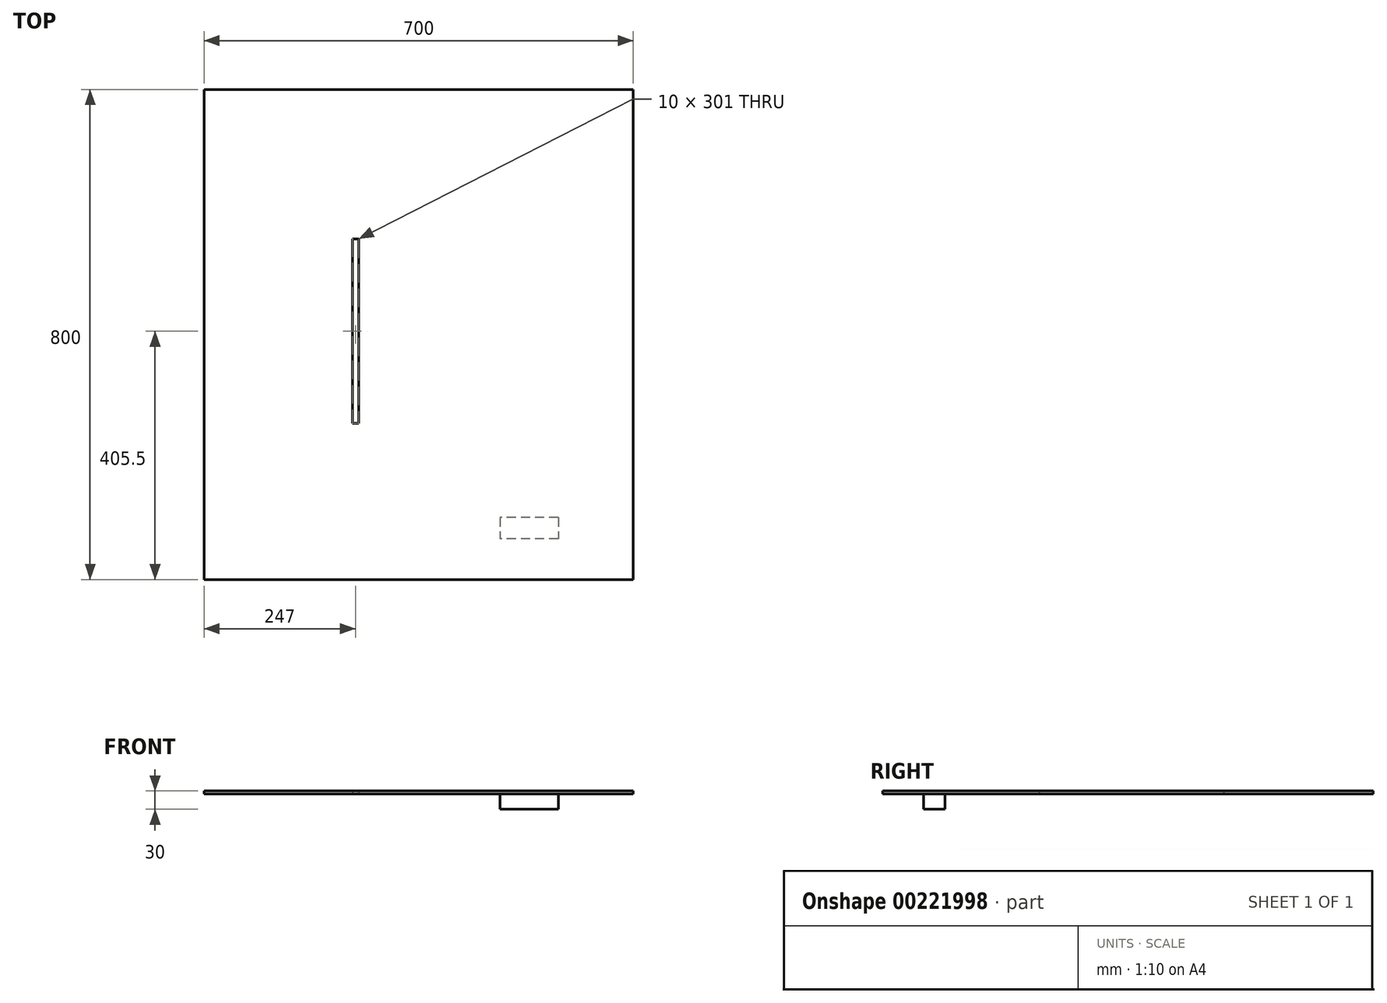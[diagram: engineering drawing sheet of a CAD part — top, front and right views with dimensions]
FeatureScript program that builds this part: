
annotation { "Feature Type Name" : "Feature", "Feature Type Description" : "" }
export const myFeature = defineFeature(function(context is Context, id is Id, definition is map)
    precondition{}
    {
        {
            var Q0;
            Q0=qCreatedBy(makeId("Top.planeOp"),FACE);
            var sketch = newSketch(context, id + "F0", { "sketchPlane" : qUnion([Q0])});
            skLineSegment(sketch, "E0.bottom", {"start": v(350, -400) * mm, "end": v(-350, -400) * mm});
            skLineSegment(sketch, "E0.top", {"start": v(350, 400) * mm, "end": v(-350, 400) * mm});
            skLineSegment(sketch, "E0.left", {"start": v(350, -400) * mm, "end": v(350, 400) * mm});
            skLineSegment(sketch, "E0.right", {"start": v(-350, -400) * mm, "end": v(-350, 400) * mm});
            skPoint(sketch, "E0.middle", {"position": v(0, 0) * mm});
            skLineSegment(sketch, "E1.bottom", {"start": v(-98, -145) * mm, "end": v(-108, -145) * mm});
            skLineSegment(sketch, "E1.top", {"start": v(-98, 156) * mm, "end": v(-108, 156) * mm});
            skLineSegment(sketch, "E1.left", {"start": v(-108, -145) * mm, "end": v(-108, 156) * mm});
            skLineSegment(sketch, "E1.right", {"start": v(-98, -145) * mm, "end": v(-98, 156) * mm});
            skPoint(sketch, "E1.middle", {"position": v(-103, 5.5) * mm});
            skSolve(sketch);
        }
        {
            var Q0;
            Q0 = qSketchRegion(id + "F0", true);
            extrude(context, id + "F1", {"entities" : qUnion([Q0]), "depth" : 5 * mm});
        }
        {
            var Q0;
            Q0=makeQuery(id+"F0.imprint","IMPRINT",FACE,{"disambiguationData":[TD([[makeQuery(id+"F0.imprint","IMPRINT",EDGE,{"derivedFrom":sQuery(id+"F0.wireOp",EDGE,"E0.bottom")}),-1.0]])]});
            var sketch = newSketch(context, id + "F2", { "sketchPlane" : qUnion([Q0])});
            skLineSegment(sketch, "E2.bottom", {"start": v(227.72, -298.49) * mm, "end": v(132.84, -298.49) * mm});
            skLineSegment(sketch, "E2.top", {"start": v(227.72, -333.57) * mm, "end": v(132.84, -333.57) * mm});
            skLineSegment(sketch, "E2.left", {"start": v(227.72, -298.49) * mm, "end": v(227.72, -333.57) * mm});
            skLineSegment(sketch, "E2.right", {"start": v(132.84, -298.49) * mm, "end": v(132.84, -333.57) * mm});
            skPoint(sketch, "E2.middle", {"position": v(180.28, -316.03) * mm});
            skSolve(sketch);
        }
        {
            var Q0;
            Q0 = qSketchRegion(id + "F2", true);
            extrude(context, id + "F3", {"entities" : qUnion([Q0]), "operationType" : NewBodyOperationType.ADD, "oppositeDirection" : true, "depth" : 25 * mm});
        }
    });
